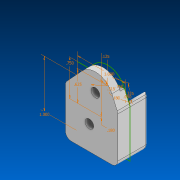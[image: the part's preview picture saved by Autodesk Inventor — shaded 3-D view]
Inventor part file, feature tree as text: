
AUTODESK INVENTOR PART (.ipt)
format: ipt  version: 2022 (Build 260153000, 153)  size: 168,960 bytes
history: native  units: in
note: dims shown in document units (in); Inventor stores cm internally (conversion verified against a paired STEP export)
features: extrude x4, fillet x3
ambient origin geometry x8: Origin, YZ Plane, XZ Plane, XY Plane, X Axis, Y Axis, Z Axis, Center Point
bodies: Solid1 (feature_tree)
feature tree (7):
  extrude  "Extrusion1"  Depth=1.0in
  extrude  "Extrusion2"  Depth=1.0in
  extrude  "Extrusion3"  Depth=0.75in
  fillet  "Fillet2"  Radius=0.335in
  fillet  "Fillet1"  Radius=0.18in
  extrude  "Extrusion4"  Depth=0.1in
  fillet  "Fillet3"  Radius=0.25in
